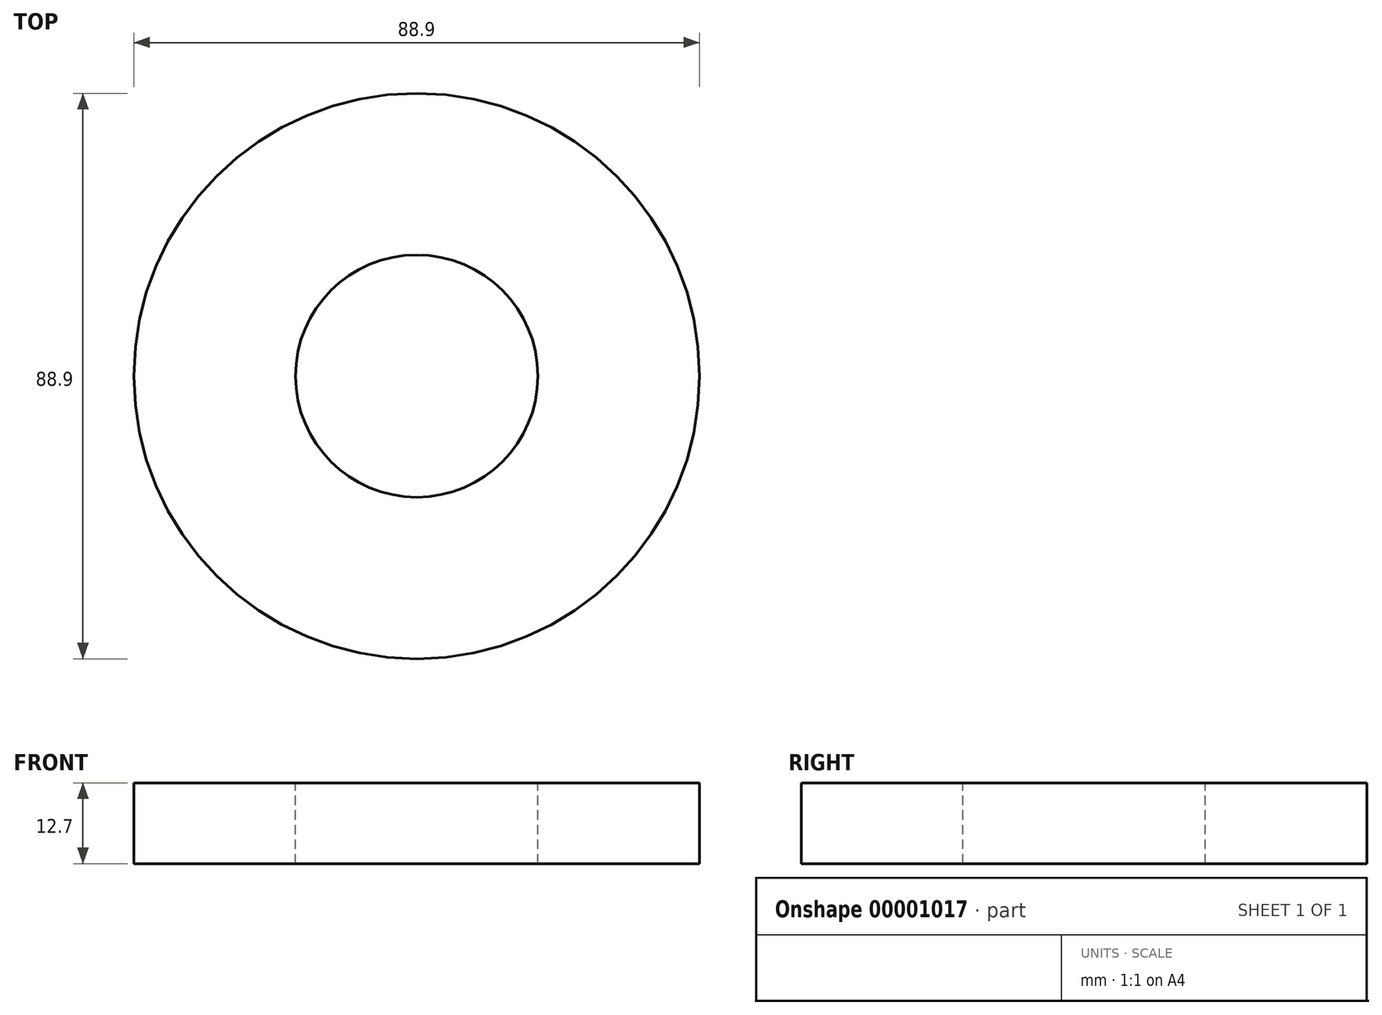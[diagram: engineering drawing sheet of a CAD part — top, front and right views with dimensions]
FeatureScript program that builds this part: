
annotation { "Feature Type Name" : "Feature", "Feature Type Description" : "" }
export const myFeature = defineFeature(function(context is Context, id is Id, definition is map)
    precondition{}
    {
        {
            var Q0;
            Q0=qCreatedBy(makeId("Top.planeOp"),FACE);
            var sketch = newSketch(context, id + "F0", { "sketchPlane" : qUnion([Q0])});
            skCircle(sketch, "E0", {"center": v(0, 0) * mm, "radius": 44.45 * mm});
            skCircle(sketch, "E1", {"center": v(0, 0) * mm, "radius": 19.05 * mm});
            skSolve(sketch);
        }
        {
            var Q0;
            Q0=makeQuery(id+"F0.imprint","IMPRINT",FACE,{"disambiguationData":[TD([[makeQuery(id+"F0.imprint","IMPRINT",EDGE,{"derivedFrom":sQuery(id+"F0.wireOp",EDGE,"E0")}),1.0]])]});
            var Q1;
            Q1=sQuery(id+"F0.wireOp",EDGE,"E0");
            var Q2;
            Q2=sQuery(id+"F0.wireOp",EDGE,"E1");
            extrude(context, id + "F1", {"entities" : qUnion([Q0]), "bodyType" : ToolBodyType.SURFACE, "surfaceEntities" : qUnion([Q1, Q2]), "depth" : 12.7 * mm});
        }
        {
            var Q0;
            Q0=qCreatedBy(makeId("Top.planeOp"),FACE);
            cPlane(context, id + "F2", {"entities" : qUnion([Q0]), "cplaneType" : CPlaneType.OFFSET, "offset" : 12.7 * mm, "width" : 152.4 * mm, "height" : 152.4 * mm});
        }
    });
